# Revit family: AOT_PRS UNI LED
name_source: partatom
category: Осветительные приборы
revit_build: Autodesk Revit 2016 (Build: 20150220_1215(x64)
units: mm (PartAtom-declared; Revit-internal decimal feet)

## family parameters
Источник света = Да
Общий = Нет
Основа = Грань
При загрузке вырезать с полостями = Нет
Размер круглого соединителя = Использовать диаметр
Тип детали = Нормальный
Точка расчета площади = Нет

## types (1)
- AOT.PRS UNI LED 1200x200 4000K
    ADSK_Единица измерения = Шт.
    ADSK_Завод-изготовитель = ООО МГК Световые технологии
    ADSK_Код изделия = 1068000030
    ADSK_Количество фаз = 1
    ADSK_Количество фаз числовое = 1
    ADSK_Коэффициент мощности = 0.98
    ADSK_Масса = 2.8
    ADSK_Наименование = Накладные светодиодные светильники для учебных и офисных помещений с засветкой как фронтальной, так и торцевой части рассеивателя. AOT.OPL UNI LED -оптимальный выбор для помещений, где необходим мягкий рассеянный свет, AOT.PRS UNI LED - для помещений, где необходима высокая энергоэффективность
    ADSK_Напряжение = 230 В
    ADSK_Номинальная мощность = 0 кВт
    ADSK_Полная мощность = 0 кВ·А
    ADSK_Размер_Длина = 1270 мм
    ADSK_Размер_Ширина = 190 мм
    ADSK_Ток = 0 А
    ADSK_Энергоэффективность = 100 лм/Вт
    IP Class = IP40
    URL = http://ltcompany.com
    Блок аварийного питания = Нет
    Видимая форма излучения при визуализации = Нет
    Группа модели = Светильники
    Длина.свет = 165 мм
    Изготовитель = ООО МГК Световые технологии
    Излучение по длине прямоугольника = 1270 мм
    Излучение по ширине прямоугольника = 190 мм
    Класс Защиты = I
    Класс пожароопасности = П-II,IIа
    Климатическая зона = УХЛ4
    Код по классификатору = D5020200
    Корпус = Нержавеющая сталь
    Область использования = ЖКХ, Лестницы/коридоры
    Описание = Накладные светодиодные светильники для учебных и офисных помещений с засветкой как фронтальной, так и торцевой части рассеивателя. AOT.OPL UNI LED -оптимальный выбор для помещений, где необходим мягкий рассеянный свет, AOT.PRS UNI LED - для помещений, где необходима высокая энергоэффективность
    Отметка по умолчанию = 0 мм
    Плафон = Плафон полупрозрачный
    Полная установленная мощность = 0 кВ·А
    Разработчик = ООО ПРОРУБИМ
    Разработчик (телефон) = +7 (495) 649-85-43
    Светофильтр = 16777215
    Смещение цветовой температуры при затухании лампы = <Нет>
    Тип ИС = LED
    Тип ПРА = Драйвер
    Тип продукции = Cветильник
    Угол наклона = -90.00°
    Файл фотометрической сетки = AOT.PRS UNI LED 1200×200 4000K.ies
    Ширина.свет = 1245 мм
